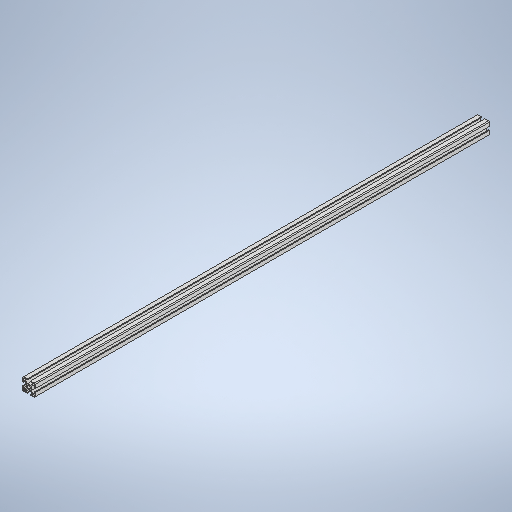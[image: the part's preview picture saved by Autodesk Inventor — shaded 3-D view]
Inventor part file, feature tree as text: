
AUTODESK INVENTOR PART (.ipt)
format: ipt  version: 2025 (Build 290162000, 162)  size: 315,392 bytes
history: native  units: in
note: dims shown in document units (in); Inventor stores cm internally (conversion verified against a paired STEP export)
features: extrude x1, sketch x1
ambient origin geometry x8: Origin, YZ Plane, XZ Plane, XY Plane, X Axis, Y Axis, Z Axis, Center Point
bodies: Solid1 (feature_tree)
feature tree (2):
  extrude  "Extrusion1"  Depth=43.3071in
  sketch  "Sketch1"  dims[d6=43.3071in d7=0.0in d8=0.1969in d9=0.0344in]
